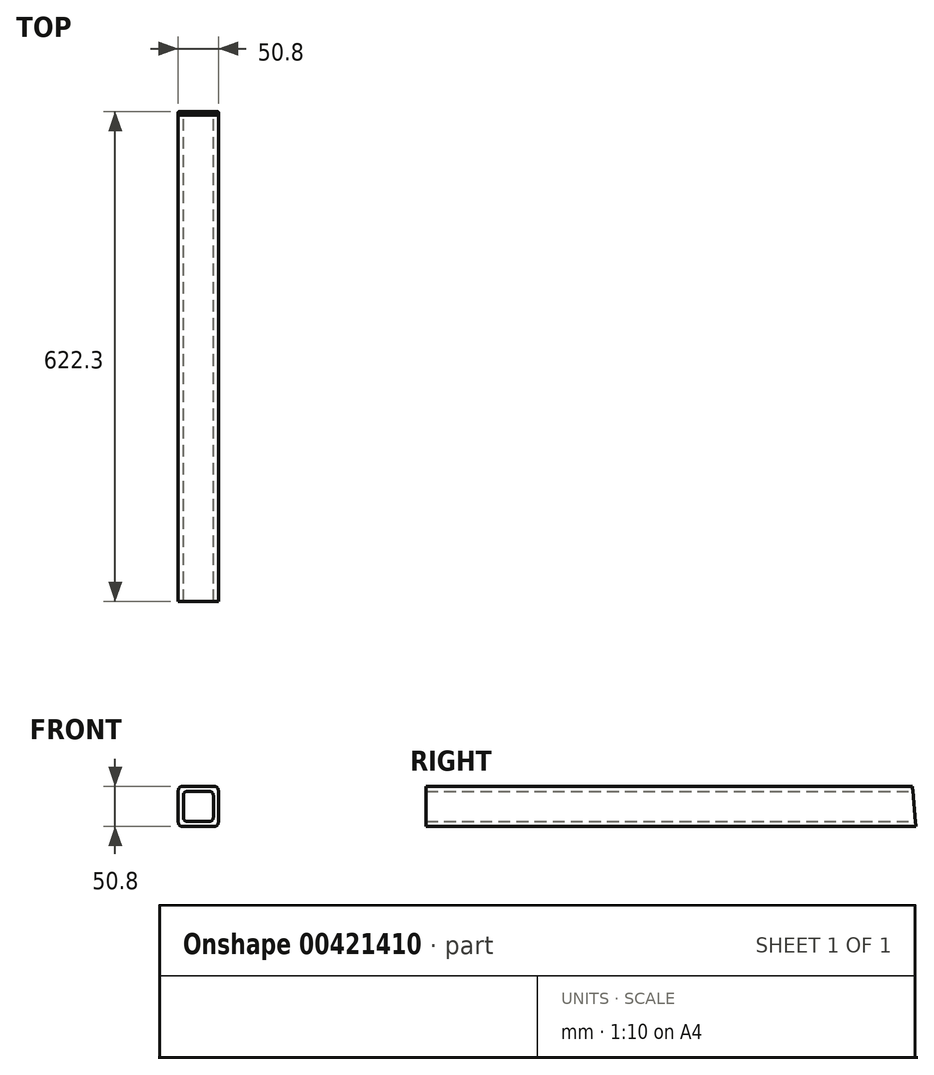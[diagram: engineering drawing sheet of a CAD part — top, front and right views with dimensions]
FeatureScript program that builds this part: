
annotation { "Feature Type Name" : "Feature", "Feature Type Description" : "" }
export const myFeature = defineFeature(function(context is Context, id is Id, definition is map)
    precondition{}
    {
        {
            var Q0;
            Q0=qCreatedBy(makeId("Front.planeOp"),FACE);
            var sketch = newSketch(context, id + "F0", { "sketchPlane" : qUnion([Q0])});
            skLineSegment(sketch, "E0.bottom", {"start": v(25.4, -25.4) * mm, "end": v(-25.4, -25.4) * mm});
            skLineSegment(sketch, "E0.top", {"start": v(25.4, 25.4) * mm, "end": v(-25.4, 25.4) * mm});
            skLineSegment(sketch, "E0.left", {"start": v(25.4, -25.4) * mm, "end": v(25.4, 25.4) * mm});
            skLineSegment(sketch, "E0.right", {"start": v(-25.4, -25.4) * mm, "end": v(-25.4, 25.4) * mm});
            skPoint(sketch, "E0.middle", {"position": v(0, 0) * mm});
            skLineSegment(sketch, "E1.bottom", {"start": v(19.05, -19.05) * mm, "end": v(-19.05, -19.05) * mm});
            skLineSegment(sketch, "E1.top", {"start": v(19.05, 19.05) * mm, "end": v(-19.05, 19.05) * mm});
            skLineSegment(sketch, "E1.left", {"start": v(19.05, -19.05) * mm, "end": v(19.05, 19.05) * mm});
            skLineSegment(sketch, "E1.right", {"start": v(-19.05, -19.05) * mm, "end": v(-19.05, 19.05) * mm});
            skSolve(sketch);
        }
        {
            var Q0;
            Q0 = qSketchRegion(id + "F0", true);
            extrude(context, id + "F1", {"entities" : qUnion([Q0]), "endBound" : BoundingType.SYMMETRIC, "depth" : 622.3 * mm});
        }
        {
            var Q0;
            Q0=makeQuery(id+"F1.opExtrude","SWEPT_FACE",FACE,{"disambiguationData":[OSD([sQuery(id+"F0.wireOp",EDGE,"E0.right")])]});
            var sketch = newSketch(context, id + "F2", { "sketchPlane" : qUnion([Q0])});
            skLineSegment(sketch, "E2", {"start": v(-311.15, 25.4) * mm, "end": v(-311.15, -25.4) * mm});
            skLineSegment(sketch, "E3", {"start": v(-311.15, -25.4) * mm, "end": v(-302.75, 70.56) * mm});
            skSolve(sketch);
        }
        {
            var Q0;
            {var subQ0=sQuery(id+"F2.wireOp",EDGE,"E2");Q0=makeQuery(id+"F2.imprint","IMPRINT",FACE,{"disambiguationData":[TD([[makeQuery(id+"F2.imprint","IMPRINT",EDGE,{"derivedFrom":subQ0}),-1.0]])]});}
            extrude(context, id + "F3", {"entities" : qUnion([Q0]), "operationType" : NewBodyOperationType.REMOVE, "oppositeDirection" : true, "depth" : 50.8 * mm});
        }
        {
            var Q0;
            Q0=makeQuery(id+"F1.opExtrude","SWEPT_EDGE",EDGE,{"disambiguationData":[OSD([sQuery(id+"F0.wireOp",EDGE,"E0.top"),sQuery(id+"F0.wireOp",EDGE,"E0.left")])]});
            var Q1;
            Q1=makeQuery(id+"F1.opExtrude","SWEPT_EDGE",EDGE,{"disambiguationData":[OSD([sQuery(id+"F0.wireOp",EDGE,"E0.top"),sQuery(id+"F0.wireOp",EDGE,"E0.right")])]});
            var Q2;
            Q2=makeQuery(id+"F1.opExtrude","SWEPT_EDGE",EDGE,{"disambiguationData":[OSD([sQuery(id+"F0.wireOp",EDGE,"E0.bottom"),sQuery(id+"F0.wireOp",EDGE,"E0.left")])]});
            var Q3;
            Q3=makeQuery(id+"F1.opExtrude","SWEPT_EDGE",EDGE,{"disambiguationData":[OSD([sQuery(id+"F0.wireOp",EDGE,"E0.bottom"),sQuery(id+"F0.wireOp",EDGE,"E0.right")])]});
            var Q4;
            Q4=makeQuery(id+"F1.opExtrude","SWEPT_EDGE",EDGE,{"disambiguationData":[OSD([sQuery(id+"F0.wireOp",EDGE,"E1.top"),sQuery(id+"F0.wireOp",EDGE,"E1.left")])]});
            var Q5;
            Q5=makeQuery(id+"F1.opExtrude","SWEPT_EDGE",EDGE,{"disambiguationData":[OSD([sQuery(id+"F0.wireOp",EDGE,"E1.top"),sQuery(id+"F0.wireOp",EDGE,"E1.right")])]});
            var Q6;
            Q6=makeQuery(id+"F1.opExtrude","SWEPT_EDGE",EDGE,{"disambiguationData":[OSD([sQuery(id+"F0.wireOp",EDGE,"E1.bottom"),sQuery(id+"F0.wireOp",EDGE,"E1.left")])]});
            var Q7;
            Q7=makeQuery(id+"F1.opExtrude","SWEPT_EDGE",EDGE,{"disambiguationData":[OSD([sQuery(id+"F0.wireOp",EDGE,"E1.bottom"),sQuery(id+"F0.wireOp",EDGE,"E1.right")])]});
            fillet(context, id + "F4", {"entities" : qUnion([Q0, Q1, Q2, Q3, Q4, Q5, Q6, Q7]), "radius" : 5.08 * mm, "tangentPropagation" : true, "allowEdgeOverflow" : false});
        }
    });
